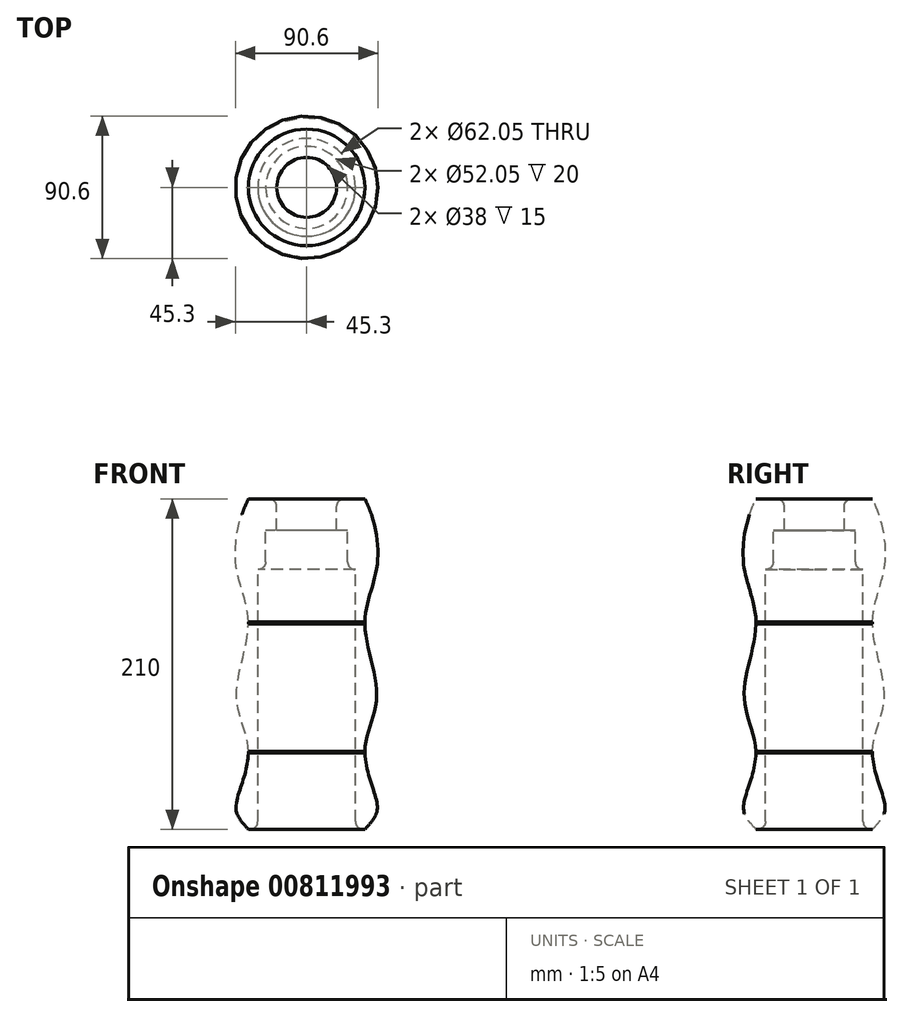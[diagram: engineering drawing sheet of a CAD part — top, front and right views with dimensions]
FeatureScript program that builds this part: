
annotation { "Feature Type Name" : "Feature", "Feature Type Description" : "" }
export const myFeature = defineFeature(function(context is Context, id is Id, definition is map)
    precondition{}
    {
        {
            var Q0;
            Q0=qCreatedBy(makeId("Front.planeOp"),FACE);
            var sketch = newSketch(context, id + "F0", { "sketchPlane" : qUnion([Q0])});
            skLineSegment(sketch, "E0", {"start": v(0, 29.06) * mm, "end": v(0, -53.53) * mm, "construction": true});
            skLineSegment(sketch, "E1", {"start": v(-26.02, 73.79) * mm, "end": v(-26.02, 98.79) * mm});
            skLineSegment(sketch, "E2", {"start": v(-26.02, 73.79) * mm, "end": v(-31.03, 73.79) * mm});
            skLineSegment(sketch, "E3", {"start": v(-26.02, 98.79) * mm, "end": v(-19, 98.79) * mm});
            skLineSegment(sketch, "E4", {"start": v(-19, 98.79) * mm, "end": v(-19, 118.79) * mm});
            skLineSegment(sketch, "E5", {"start": v(-19, 118.79) * mm, "end": v(-37, 118.79) * mm});
            skPoint(sketch, "E6", {"position": v(-56.54, 73.79) * mm});
            skPoint(sketch, "E7", {"position": v(-56.54, 118.79) * mm});
            skLineSegment(sketch, "E8", {"start": v(-41.08, 108.79) * mm, "end": v(-36.02, 108.79) * mm});
            skPoint(sketch, "E9.end.orphan", {"position": v(-44.5, 118.79) * mm});
            skPoint(sketch, "E9.start.orphan", {"position": v(-87.06, 73.79) * mm});
            skLineSegment(sketch, "E10", {"start": v(-37, 108.79) * mm, "end": v(-37, 118.79) * mm});
            skLineSegment(sketch, "E11", {"start": v(0, 40.86) * mm, "end": v(0, -55.83) * mm, "construction": true});
            skLineSegment(sketch, "E12", {"start": v(-37, 40.46) * mm, "end": v(-37, -91.21) * mm});
            skLineSegment(sketch, "E13", {"start": v(-37, -91.21) * mm, "end": v(-31.03, -91.21) * mm});
            skLineSegment(sketch, "E14", {"start": v(-31.03, -81.21) * mm, "end": v(-65.9, -81.21) * mm});
            skLineSegment(sketch, "E15", {"start": v(0, -34.92) * mm, "end": v(0, -113.85) * mm, "construction": true});
            skFitSpline(sketch, "E16", {"points": [v(-37, 118.79) * mm, v(-44.5, 74.67) * mm, v(-37, 39.18) * mm, v(-44.5, -7.22) * mm, v(-37, -41.74) * mm, v(-44.5, -73.6) * mm, v(-37, -91.21) * mm], "startDerivative": vector(-117.68, -247.12) * mm, "endDerivative": vector(183.13, -197.97) * mm});
            skLineSegment(sketch, "E17", {"start": v(-44.5, 94.99) * mm, "end": v(-44.5, -91.32) * mm, "construction": true});
            skLineSegment(sketch, "E18", {"start": v(-31.03, 73.79) * mm, "end": v(-31.03, -81.21) * mm});
            skPoint(sketch, "E19.orphan", {"position": v(-65.9, 108.79) * mm});
            skLineSegment(sketch, "E20", {"start": v(-31.03, -74.61) * mm, "end": v(-31.03, -91.21) * mm});
            skSolve(sketch);
        }
        {
            var Q0;
            Q0 = qSketchRegion(id + "F0", true);
            var Q1;
            Q1=sQuery(id+"F0.wireOp",EDGE,"E11");
            revolve(context, id + "F1", {"surfaceOperationType" : NewSurfaceOperationType.NEW, "entities" : qUnion([Q0]), "axis" : qUnion([Q1]), "revolveType" : RevolveType.FULL});
        }
        {
            var Q0;
            Q0=makeQuery(id+"F1.opRevolve","SWEPT_EDGE",EDGE,{"disambiguationData":[OSD([sQuery(id+"F0.wireOp",EDGE,"E1"),sQuery(id+"F0.wireOp",EDGE,"E2")])]});
            fillet(context, id + "F2", {"entities" : qUnion([Q0]), "radius" : 5 * mm, "tangentPropagation" : true, "allowEdgeOverflow" : false});
        }
        {
            var Q0;
            Q0=makeQuery(id+"F1.opRevolve","SWEPT_EDGE",EDGE,{"disambiguationData":[OSD([sQuery(id+"F0.wireOp",EDGE,"E4"),sQuery(id+"F0.wireOp",EDGE,"E5")])]});
            var Q1;
            Q1=makeQuery(id+"F1.opRevolve","SWEPT_EDGE",EDGE,{"disambiguationData":[OSD([sQuery(id+"F0.wireOp",EDGE,"E13"),sQuery(id+"F0.wireOp",EDGE,"E20")])]});
            fillet(context, id + "F3", {"entities" : qUnion([Q0, Q1]), "radius" : 5 * mm, "tangentPropagation" : true, "allowEdgeOverflow" : false});
        }
        {
            var Q0;
            Q0=makeQuery(id+"F1.opRevolve","SWEPT_BODY",BODY,{"disambiguationData":[OSD([sQuery(id+"F0.wireOp",EDGE,"E1"),sQuery(id+"F0.wireOp",EDGE,"E2"),sQuery(id+"F0.wireOp",EDGE,"E3"),sQuery(id+"F0.wireOp",EDGE,"E4"),sQuery(id+"F0.wireOp",EDGE,"E5"),sQuery(id+"F0.wireOp",EDGE,"E12"),sQuery(id+"F0.wireOp",EDGE,"E13"),sQuery(id+"F0.wireOp",EDGE,"E16"),sQuery(id+"F0.wireOp",EDGE,"E18"),sQuery(id+"F0.wireOp",EDGE,"E20")])]});
            transform(context, id + "F4", {"entities" : qUnion([Q0]), "transformType" : TransformType.TRANSLATION_3D, "dx" : 0 * mm, "dy" : 0 * mm, "dz" : 0 * mm, "makeCopy" : true});
        }
    });
